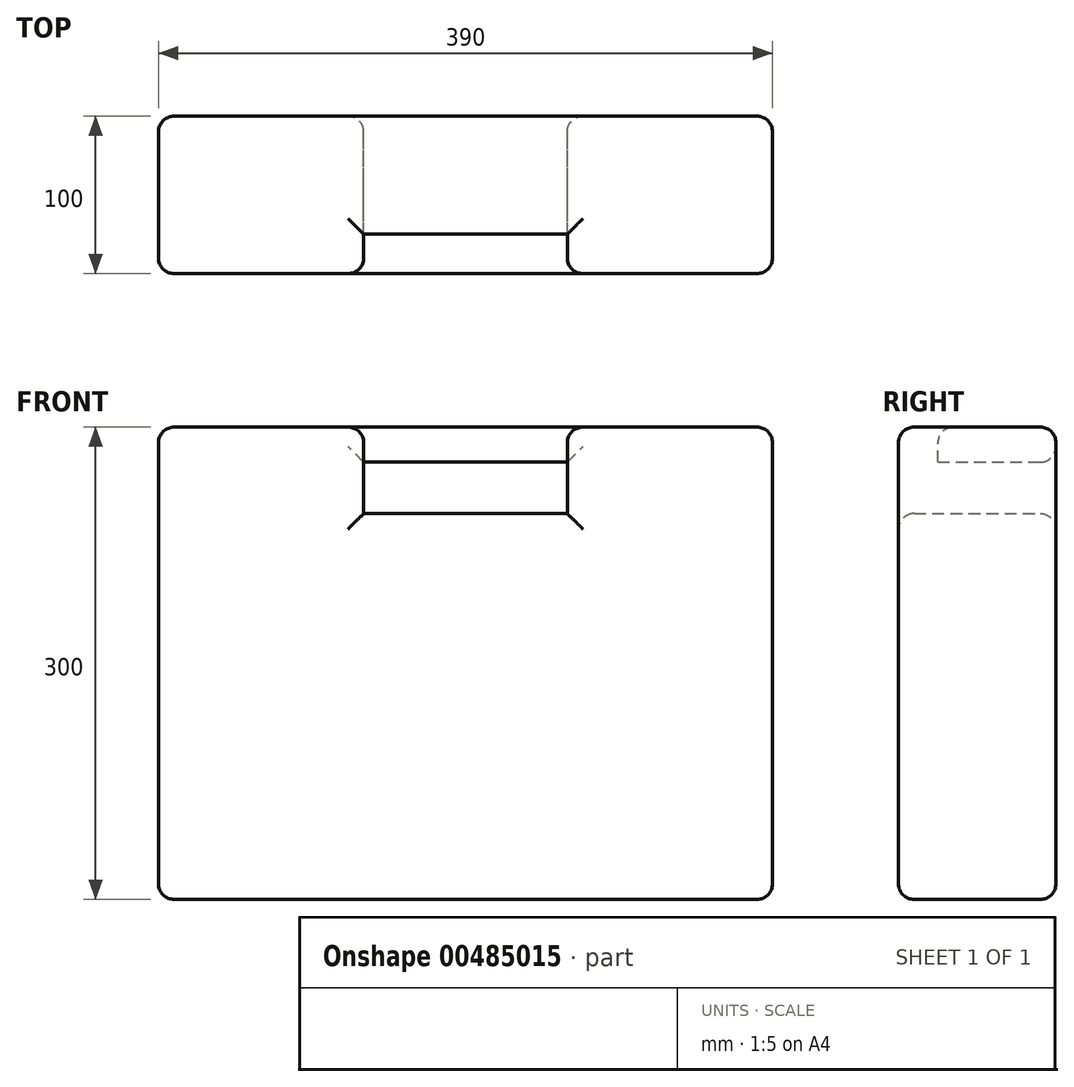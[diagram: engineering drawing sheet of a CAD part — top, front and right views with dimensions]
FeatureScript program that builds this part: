
annotation { "Feature Type Name" : "Feature", "Feature Type Description" : "" }
export const myFeature = defineFeature(function(context is Context, id is Id, definition is map)
    precondition{}
    {
        {
            var Q0;
            Q0=qCreatedBy(makeId("Front.planeOp"),FACE);
            var sketch = newSketch(context, id + "F0", { "sketchPlane" : qUnion([Q0])});
            skLineSegment(sketch, "E0.bottom", {"start": v(195, 150) * mm, "end": v(-195, 150) * mm});
            skLineSegment(sketch, "E0.top", {"start": v(195, -150) * mm, "end": v(-195, -150) * mm});
            skLineSegment(sketch, "E0.left", {"start": v(195, 150) * mm, "end": v(195, -150) * mm});
            skLineSegment(sketch, "E0.right", {"start": v(-195, 150) * mm, "end": v(-195, -150) * mm});
            skPoint(sketch, "E0.middle", {"position": v(0, 0) * mm});
            skLineSegment(sketch, "E1.bottom", {"start": v(64.64, 95.1) * mm, "end": v(-64.64, 95.1) * mm});
            skLineSegment(sketch, "E1.top", {"start": v(64.64, 127.67) * mm, "end": v(-64.64, 127.67) * mm});
            skLineSegment(sketch, "E1.left", {"start": v(64.64, 95.1) * mm, "end": v(64.64, 127.67) * mm});
            skLineSegment(sketch, "E1.right", {"start": v(-64.64, 95.1) * mm, "end": v(-64.64, 127.67) * mm});
            skPoint(sketch, "E1.middle", {"position": v(0, 111.38) * mm});
            skSolve(sketch);
        }
        {
            var Q0;
            Q0=makeQuery(id+"F0.imprint","IMPRINT",FACE,{"disambiguationData":[TD([[makeQuery(id+"F0.imprint","IMPRINT",EDGE,{"derivedFrom":sQuery(id+"F0.wireOp",EDGE,"E0.bottom")}),1.0]])]});
            extrude(context, id + "F1", {"entities" : qUnion([Q0]), "endBound" : BoundingType.SYMMETRIC, "depth" : 100 * mm, "offsetDistance" : 25 * mm});
        }
        {
            var Q0;
            Q0=makeQuery(id+"F1.opExtrude","CAP_FACE",FACE,{"disambiguationData":[OSD([sQuery(id+"F0.wireOp",EDGE,"E0.bottom"),sQuery(id+"F0.wireOp",EDGE,"E0.top"),sQuery(id+"F0.wireOp",EDGE,"E0.left"),sQuery(id+"F0.wireOp",EDGE,"E0.right"),sQuery(id+"F0.wireOp",EDGE,"E1.bottom"),sQuery(id+"F0.wireOp",EDGE,"E1.top"),sQuery(id+"F0.wireOp",EDGE,"E1.left"),sQuery(id+"F0.wireOp",EDGE,"E1.right")])],"isStart":false});
            var sketch = newSketch(context, id + "F2", { "sketchPlane" : qUnion([Q0])});
            skLineSegment(sketch, "E2.bottom", {"start": v(-64.64, 127.67) * mm, "end": v(64.64, 127.67) * mm});
            skLineSegment(sketch, "E2.top", {"start": v(-64.64, 150) * mm, "end": v(64.64, 150) * mm});
            skLineSegment(sketch, "E2.left", {"start": v(-64.64, 127.67) * mm, "end": v(-64.64, 150) * mm});
            skLineSegment(sketch, "E2.right", {"start": v(64.64, 127.67) * mm, "end": v(64.64, 150) * mm});
            skSolve(sketch);
        }
        {
            var Q0;
            Q0=makeQuery(id+"F2.imprint","IMPRINT",FACE,{"disambiguationData":[TD([[makeQuery(id+"F2.imprint","IMPRINT",EDGE,{"derivedFrom":sQuery(id+"F2.wireOp",EDGE,"E2.bottom")}),-1.0]])]});
            extrude(context, id + "F3", {"entities" : qUnion([Q0]), "operationType" : NewBodyOperationType.REMOVE, "oppositeDirection" : true, "depth" : 25 * mm, "offsetDistance" : 25 * mm});
        }
        {
            var Q0;
            Q0=makeQuery(id+"F1.opExtrude","CAP_FACE",FACE,{"disambiguationData":[OSD([sQuery(id+"F0.wireOp",EDGE,"E0.bottom"),sQuery(id+"F0.wireOp",EDGE,"E0.top"),sQuery(id+"F0.wireOp",EDGE,"E0.left"),sQuery(id+"F0.wireOp",EDGE,"E0.right"),sQuery(id+"F0.wireOp",EDGE,"E1.bottom"),sQuery(id+"F0.wireOp",EDGE,"E1.top"),sQuery(id+"F0.wireOp",EDGE,"E1.left"),sQuery(id+"F0.wireOp",EDGE,"E1.right")])],"isStart":false});
            var Q1;
            Q1=makeQuery(id+"F1.opExtrude","SWEPT_FACE",FACE,{"disambiguationData":[OSD([sQuery(id+"F0.wireOp",EDGE,"E0.right")])]});
            var Q2;
            Q2=makeQuery(id+"F1.opExtrude","SWEPT_FACE",FACE,{"disambiguationData":[OSD([sQuery(id+"F0.wireOp",EDGE,"E0.bottom")])]});
            var Q3;
            Q3=makeQuery(id+"F1.opExtrude","CAP_FACE",FACE,{"disambiguationData":[OSD([sQuery(id+"F0.wireOp",EDGE,"E0.bottom"),sQuery(id+"F0.wireOp",EDGE,"E0.top"),sQuery(id+"F0.wireOp",EDGE,"E0.left"),sQuery(id+"F0.wireOp",EDGE,"E0.right"),sQuery(id+"F0.wireOp",EDGE,"E1.bottom"),sQuery(id+"F0.wireOp",EDGE,"E1.top"),sQuery(id+"F0.wireOp",EDGE,"E1.left"),sQuery(id+"F0.wireOp",EDGE,"E1.right")])],"isStart":true});
            var Q4;
            Q4=makeQuery(id+"F1.opExtrude","SWEPT_FACE",FACE,{"disambiguationData":[OSD([sQuery(id+"F0.wireOp",EDGE,"E0.top")])]});
            fillet(context, id + "F4", {"entities" : qUnion([Q0, Q1, Q2, Q3, Q4]), "radius" : 10 * mm, "tangentPropagation" : true, "allowEdgeOverflow" : false});
        }
    });
